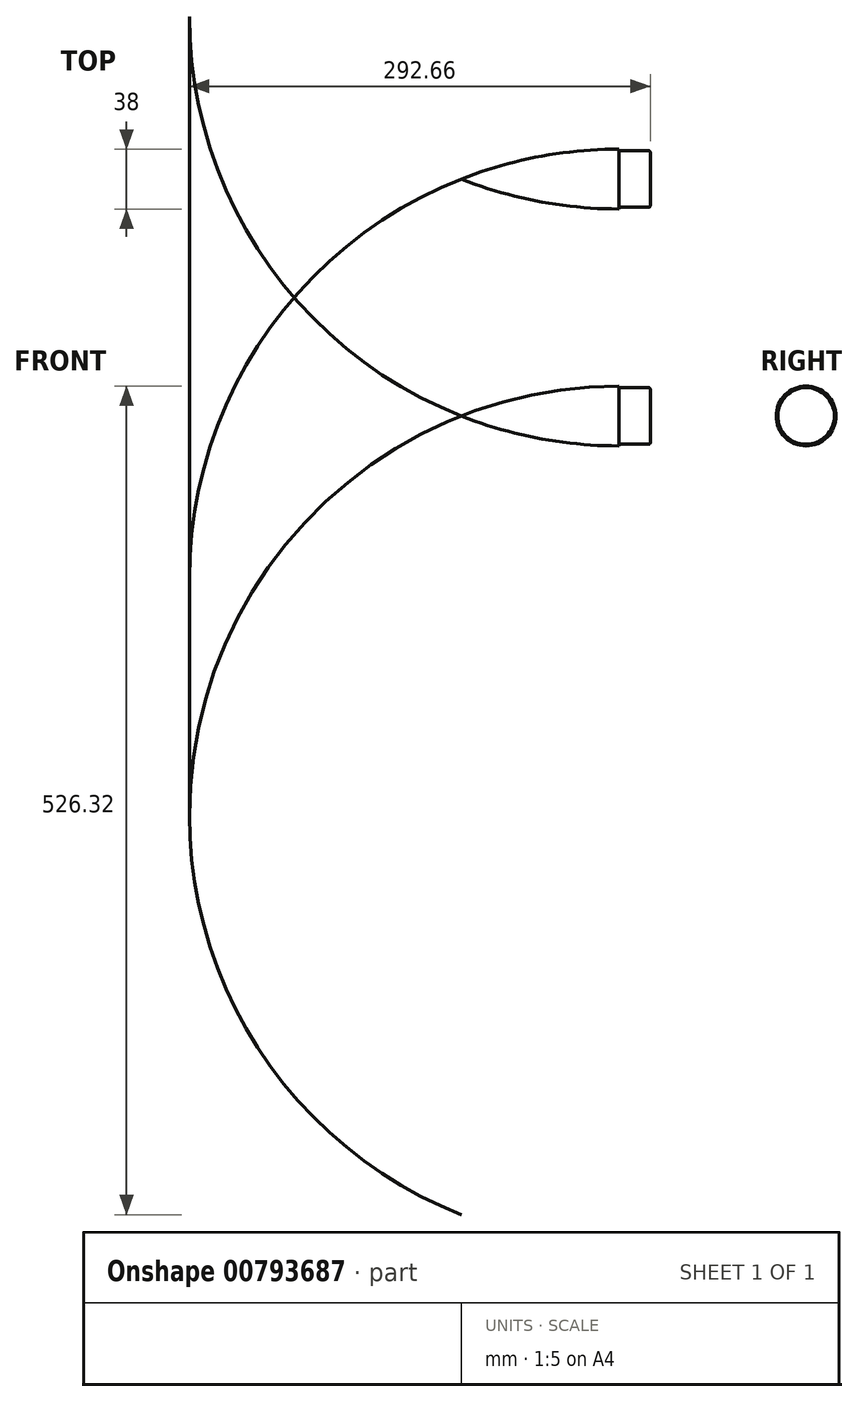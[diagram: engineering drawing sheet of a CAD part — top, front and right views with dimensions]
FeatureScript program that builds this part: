
annotation { "Feature Type Name" : "Feature", "Feature Type Description" : "" }
export const myFeature = defineFeature(function(context is Context, id is Id, definition is map)
    precondition{}
    {
        {
            var Q0;
            Q0=qCreatedBy(makeId("Top.planeOp"),FACE);
            var sketch = newSketch(context, id + "F0", { "sketchPlane" : qUnion([Q0])});
            skLineSegment(sketch, "E0", {"start": v(100, 0) * mm, "end": v(-49.92, 0) * mm, "construction": true});
            skLineSegment(sketch, "E1", {"start": v(0, 0) * mm, "end": v(0, 19) * mm, "construction": true});
            skLineSegment(sketch, "E2", {"start": v(100, 0) * mm, "end": v(100, 19) * mm, "construction": true});
            skLineSegment(sketch, "E3", {"start": v(-37.94, 19) * mm, "end": v(86.47, 19) * mm, "construction": true});
            skLineSegment(sketch, "E4.bottom", {"start": v(100, 18) * mm, "end": v(119, 18) * mm});
            skLineSegment(sketch, "E4.right", {"start": v(120, 17) * mm, "end": v(120, 0) * mm});
            skLineSegment(sketch, "E5", {"start": v(100, 19) * mm, "end": v(100, 18) * mm});
            skLineSegment(sketch, "E6", {"start": v(0, 0) * mm, "end": v(120, 0) * mm});
            skLineSegment(sketch, "E7.left", {"start": v(100, 19) * mm, "end": v(100, 19) * mm});
            skLineSegment(sketch, "E8.bottom", {"start": v(0, 0) * mm, "end": v(115, 0) * mm});
            skLineSegment(sketch, "E8.left", {"start": v(0, 0) * mm, "end": v(0, 14.5) * mm});
            skPoint(sketch, "E9.visualSharp", {"position": v(120, 18) * mm});
            skArc(sketch, "E9.filletArc", {"start": v(120, 17) * mm, "mid": v(119.7, 17.7) * mm, "end": v(119, 18) * mm});
            skSolve(sketch);
        }
        {
            var Q0;
            Q0=qCreatedBy(makeId("Top.planeOp"),FACE);
            var sketch = newSketch(context, id + "F1", { "sketchPlane" : qUnion([Q0])});
            skLineSegment(sketch, "E10.0", {"start": v(100, 0) * mm, "end": v(-49.92, 0) * mm});
            skLineSegment(sketch, "E10.1", {"start": v(0, 0) * mm, "end": v(0, 19) * mm});
            skLineSegment(sketch, "E10.2", {"start": v(100, 0) * mm, "end": v(100, 19) * mm});
            skLineSegment(sketch, "E10.4", {"start": v(100, 18) * mm, "end": v(119, 18) * mm});
            skLineSegment(sketch, "E10.5", {"start": v(120, 17) * mm, "end": v(120, 0) * mm});
            skLineSegment(sketch, "E10.6", {"start": v(100, 19) * mm, "end": v(100, 18) * mm});
            skLineSegment(sketch, "E10.7", {"start": v(0, 0) * mm, "end": v(120, 0) * mm});
            skPoint(sketch, "E10.8", {"position": v(100, 19) * mm});
            skLineSegment(sketch, "E10.9", {"start": v(0, 0) * mm, "end": v(115, 0) * mm});
            skLineSegment(sketch, "E10.10", {"start": v(0, 0) * mm, "end": v(0, 14.5) * mm});
            skPoint(sketch, "E11.11", {"position": v(120, 18) * mm});
            skArc(sketch, "E11.12", {"start": v(120, 17) * mm, "mid": v(119.7, 17.7) * mm, "end": v(119, 18) * mm});
            skLineSegment(sketch, "E12", {"start": v(100, 19) * mm, "end": v(29.68, 19) * mm, "construction": true});
            skCircle(sketch, "E13", {"center": v(100, -253.66) * mm, "radius": 272.66 * mm});
            skSolve(sketch);
        }
        {
            var Q0;
            {var subQ0=sQuery(id+"F1.wireOp",EDGE,"E10.2");Q0=makeQuery(id+"F1.imprint","IMPRINT",FACE,{"disambiguationData":[TD([[makeQuery(id+"F1.imprint","IMPRINT",EDGE,{"derivedFrom":subQ0}),1.0]])]});}
            var Q1;
            {var subQ2=sQuery(id+"F1.wireOp",EDGE,"E10.2");Q1=makeQuery(id+"F1.imprint","IMPRINT",FACE,{"disambiguationData":[TD([[makeQuery(id+"F1.imprint","IMPRINT",EDGE,{"derivedFrom":subQ2}),-1.0]])]});}
            var Q2;
            Q2=sQuery(id+"F1.wireOp",EDGE,"E10.0");
            revolve(context, id + "F2", {"surfaceOperationType" : NewSurfaceOperationType.NEW, "entities" : qUnion([Q0, Q1]), "axis" : qUnion([Q2]), "revolveType" : RevolveType.FULL});
        }
    });
